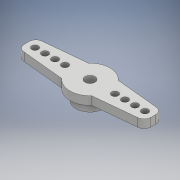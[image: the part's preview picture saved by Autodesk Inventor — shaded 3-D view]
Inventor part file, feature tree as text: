
AUTODESK INVENTOR PART (.ipt)
format: ipt  version: 2018.3 (Build 223284000, 284)  size: 167,936 bytes
history: native  units: mm
features: chamfer x4, extrude x3, sketch x3, fillet x1
ambient origin geometry x8: Origin, YZ Plane, XZ Plane, XY Plane, X Axis, Y Axis, Z Axis, Center Point
bodies: Solid1 (feature_tree)
feature tree (11):
  extrude  "Extrusion1"  Depth=3.0mm
  fillet  "Fillet1"  Radius=17.5mm
  chamfer  "Chamfer6"  Distance=2.5mm
  chamfer  "Chamfer7"  Distance=1.5mm Angle=45.0deg
  chamfer  "Chamfer8"  Distance=1.5mm Angle=45.0deg
  chamfer  "Chamfer9"  Distance=1.5mm Angle=45.0deg
  extrude  "Extrusion3"  Depth=1.5mm TaperAngle=45.0deg
  extrude  "Extrusion4"  Depth=2.0mm
  sketch  "Sketch1"  dims[d0=3.0mm d1=12.0mm d2=17.5mm]
  sketch  "Sketch3"  dims[d3=5.5mm d4=2.5mm d5=0.0mm]
  sketch  "Sketch4"  dims[d18=2.0mm d22=11.6666mm d23=1.5mm d24=45.0deg d25=11.6666mm d26=1.5mm d27=45.0deg d28=11.6666mm d29=1.5mm d30=45.0deg d31=11.6666mm d32=1.5mm d33=45.0deg d37=2.0mm d38=7.5mm d39=40.0mm d41=3.0mm d42=10.0mm d44=10.0mm d46=2.0mm d47=0.0mm d48=5.0mm d49=8.5mm d50=3.0mm d51=0.0mm]
